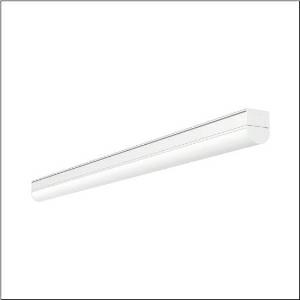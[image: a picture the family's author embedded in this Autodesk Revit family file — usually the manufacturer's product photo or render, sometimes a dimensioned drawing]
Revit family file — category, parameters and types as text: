
# Revit family: ecopack_r__31_51lj12mnm70a_41d1
name_source: partatom
category: Lighting Fixtures
units: mm (PartAtom-declared; Revit-internal decimal feet)

## family parameters
Cut with Voids When Loaded = No
Host = Face
Light Source = No
Part Type = Normal
Room Calculation Point = No
Round Connector Dimension = Use Diameter
Shared = No

## types (1)
- --- (1 x LED, 6780 lm, 50 W, 5000K)
    Apparent Load = 50 VA
    CIE Flux Codes = 39 67 87 89 100
    Color Rendering = 80
    Color Temperature = 5000K
    Default Elevation = 1800 mm
    Description = Ecopack® 31, diffuser luminaire, primary optical cover: cover, of PC, frosted, light emission: direct distribution, primary light characteristic: symmetric, installation type: surface-mounted, LED, rated luminous flux: 7.000lm, luminous efficacy: 140lm/W, light colour: 830/840/850, colour temperature: 3000/4000/5000K, control gear: ECG, with terminal, 3-pole, mains connection: 220..240V, AC, 50/60Hz, rated input power: 50W, housing, of aluminium, traffic white (RAL 9016), length: 1.450mm, width: 56mm, height: 68mm, end cap, of PC, white, protection rating (complete): IP20, insulation class (complete): insulation class I (protective earthing), certification: CE, impact resistance: IK06, permissible operating ambient temperature: -20..+40°C, packaging unit: 1 piece
    Height = 68 mm
    Lamp = 1 x LED
    Lamp Light Flux = 6780 lm
    Lamp Power = 50 W
    Lamp count = 1
    Length = 1450 mm
    Luminous efficacy = 136 lm/W
    Manufacturer = Siteco
    ModVariant = No
    Model = 51LJ12MNM70A
    Mounting Place = Ceiling
    Mounting Type = Surface mounted
    Number of Poles = 1
    OnlyDefault = Yes
    Power Factor = 1
    Product Name = Ecopack® 31
    Product group = diffuser luminaire
    ProductGroupID = 303
    Protection Class = Protection class I
    Protection Degree = IP 20
    RLX_Detail_Level = 1
    RlxData = <blob elided: 39457 chars, md5=eee3eed3>
    Socket = socket
    Standby Power = 0 W
    System Light Flux = 6780 lm
    System Power = 50 W
    Type Comments = individual setting: colour temperature 5000K, luminous flux: 100 % | (ON | ON)
    Type Image = l_1007033.jpg
    URL = http://relux.com
    VarID = @adj_086299
    Voltage = 0 V
    Weight = 0.00 kg
    Width = 56 mm

## geometry (parser evidence)
native form markers: Blend x4, Sweep x10
no freeform markers — native parametric forms only
